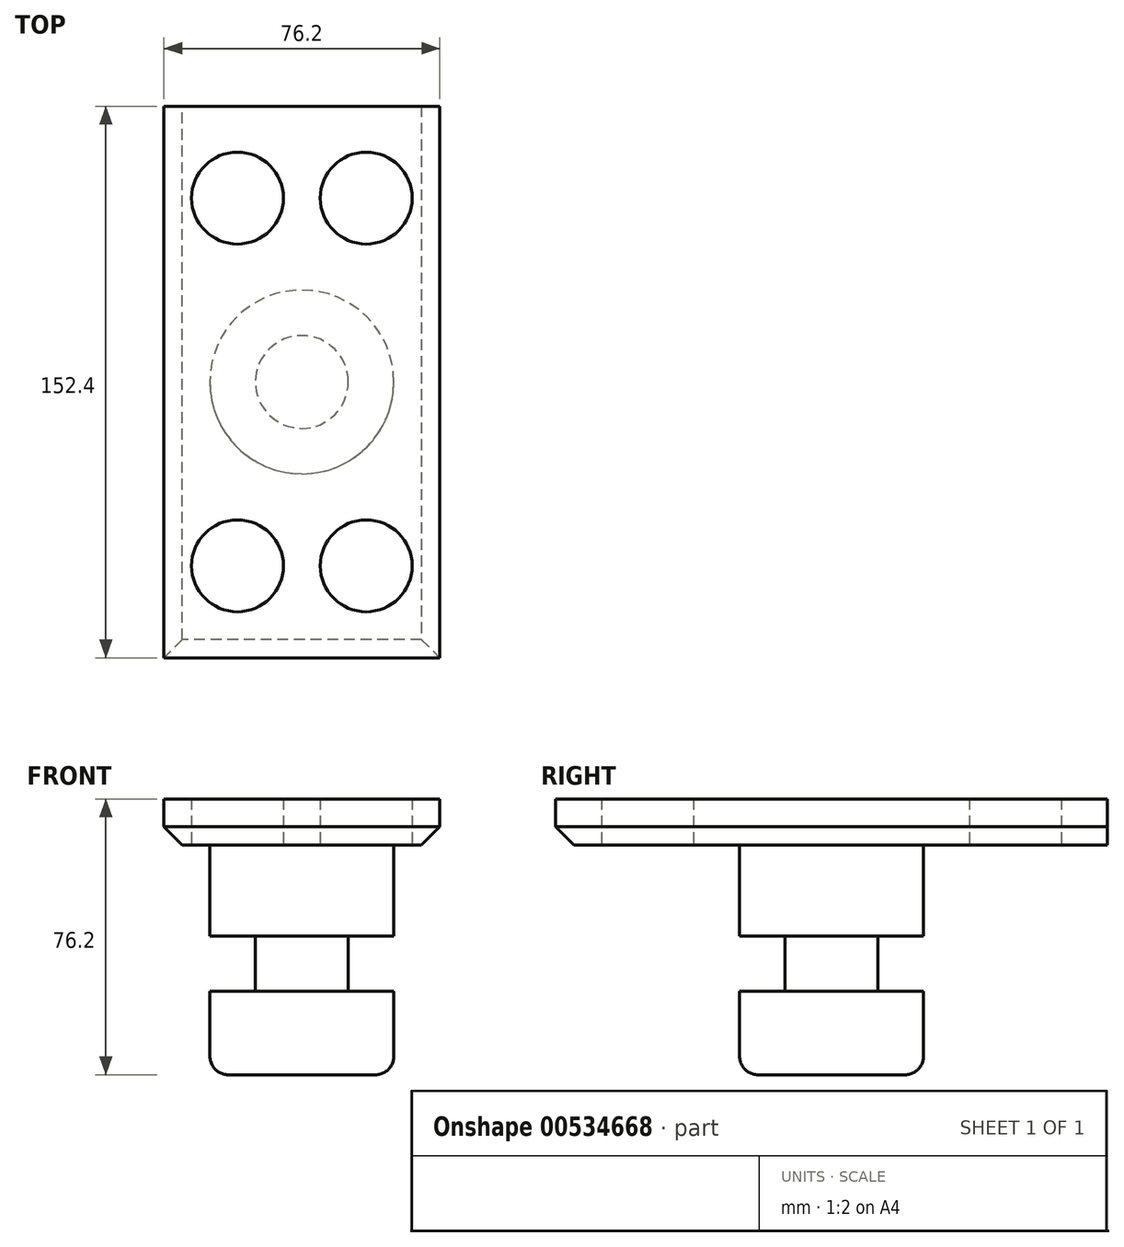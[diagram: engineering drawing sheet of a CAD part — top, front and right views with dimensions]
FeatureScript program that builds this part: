
annotation { "Feature Type Name" : "Feature", "Feature Type Description" : "" }
export const myFeature = defineFeature(function(context is Context, id is Id, definition is map)
    precondition{}
    {
        {
            var Q0;
            Q0=qCreatedBy(makeId("Top.planeOp"),FACE);
            var sketch = newSketch(context, id + "F0", { "sketchPlane" : qUnion([Q0])});
            skLineSegment(sketch, "E0.bottom", {"start": v(38.1, 76.2) * mm, "end": v(-38.1, 76.2) * mm});
            skLineSegment(sketch, "E0.top", {"start": v(38.1, -76.2) * mm, "end": v(-38.1, -76.2) * mm});
            skLineSegment(sketch, "E0.left", {"start": v(38.1, 76.2) * mm, "end": v(38.1, -76.2) * mm});
            skLineSegment(sketch, "E0.right", {"start": v(-38.1, 76.2) * mm, "end": v(-38.1, -76.2) * mm});
            skPoint(sketch, "E0.middle", {"position": v(0, 0) * mm});
            skSolve(sketch);
        }
        {
            var Q0;
            Q0 = qSketchRegion(id + "F0", true);
            extrude(context, id + "F1", {"entities" : qUnion([Q0]), "depth" : 12.7 * mm, "offsetDistance" : 25.4 * mm});
        }
        {
            var Q0;
            Q0=qCreatedBy(makeId("Top.planeOp"),FACE);
            var sketch = newSketch(context, id + "F2", { "sketchPlane" : qUnion([Q0])});
            skCircle(sketch, "E1", {"center": v(-17.78, 50.8) * mm, "radius": 12.7 * mm});
            skCircle(sketch, "E2", {"center": v(-17.78, -50.8) * mm, "radius": 12.7 * mm});
            skCircle(sketch, "E3", {"center": v(17.78, -50.8) * mm, "radius": 12.7 * mm});
            skCircle(sketch, "E4", {"center": v(17.78, 50.8) * mm, "radius": 12.7 * mm});
            skSolve(sketch);
        }
        {
            var Q0;
            Q0=makeQuery(id+"F2.imprint","IMPRINT",FACE,{"disambiguationData":[TD([[makeQuery(id+"F2.imprint","IMPRINT",EDGE,{"derivedFrom":sQuery(id+"F2.wireOp",EDGE,"E1")}),1.0]])]});
            var Q1;
            Q1=makeQuery(id+"F2.imprint","IMPRINT",FACE,{"disambiguationData":[TD([[makeQuery(id+"F2.imprint","IMPRINT",EDGE,{"derivedFrom":sQuery(id+"F2.wireOp",EDGE,"E4")}),1.0]])]});
            var Q2;
            Q2=makeQuery(id+"F2.imprint","IMPRINT",FACE,{"disambiguationData":[TD([[makeQuery(id+"F2.imprint","IMPRINT",EDGE,{"derivedFrom":sQuery(id+"F2.wireOp",EDGE,"E2")}),1.0]])]});
            var Q3;
            Q3=makeQuery(id+"F2.imprint","IMPRINT",FACE,{"disambiguationData":[TD([[makeQuery(id+"F2.imprint","IMPRINT",EDGE,{"derivedFrom":sQuery(id+"F2.wireOp",EDGE,"E3")}),1.0]])]});
            extrude(context, id + "F3", {"entities" : qUnion([Q0, Q1, Q2, Q3]), "operationType" : NewBodyOperationType.REMOVE, "endBound" : BoundingType.UP_TO_NEXT, "depth" : 25.4 * mm, "offsetDistance" : 25.4 * mm});
        }
        {
            var Q0;
            Q0=qCreatedBy(makeId("Right.planeOp"),FACE);
            var sketch = newSketch(context, id + "F4", { "sketchPlane" : qUnion([Q0])});
            skLineSegment(sketch, "E5.bottom", {"start": v(0, -63.5) * mm, "end": v(25.4, -63.5) * mm});
            skLineSegment(sketch, "E5.top", {"start": v(0, 0) * mm, "end": v(25.4, 0) * mm});
            skLineSegment(sketch, "E5.left", {"start": v(0, -63.5) * mm, "end": v(0, 0) * mm});
            skLineSegment(sketch, "E5.right", {"start": v(25.4, -63.5) * mm, "end": v(25.4, 0) * mm});
            skSolve(sketch);
        }
        {
            var Q0;
            Q0=makeQuery(id+"F4.imprint","IMPRINT",FACE,{"disambiguationData":[TD([[makeQuery(id+"F4.imprint","IMPRINT",EDGE,{"derivedFrom":sQuery(id+"F4.wireOp",EDGE,"E5.bottom")}),1.0]])]});
            var Q1;
            Q1=sQuery(id+"F4.wireOp",EDGE,"E5.left");
            revolve(context, id + "F5", {"operationType" : NewBodyOperationType.ADD, "entities" : qUnion([Q0]), "axis" : qUnion([Q1]), "revolveType" : RevolveType.FULL});
        }
        {
            var Q0;
            Q0=qCreatedBy(makeId("Right.planeOp"),FACE);
            var sketch = newSketch(context, id + "F6", { "sketchPlane" : qUnion([Q0])});
            skLineSegment(sketch, "E6.bottom", {"start": v(12.82, -40.48) * mm, "end": v(30.6, -40.48) * mm});
            skLineSegment(sketch, "E6.top", {"start": v(12.82, -25.24) * mm, "end": v(30.6, -25.24) * mm});
            skLineSegment(sketch, "E6.left", {"start": v(12.82, -40.48) * mm, "end": v(12.82, -25.24) * mm});
            skLineSegment(sketch, "E6.right", {"start": v(30.6, -40.48) * mm, "end": v(30.6, -25.24) * mm});
            skSolve(sketch);
        }
        {
            var Q0;
            Q0=makeQuery(id+"F6.imprint","IMPRINT",FACE,{"disambiguationData":[TD([[makeQuery(id+"F6.imprint","IMPRINT",EDGE,{"derivedFrom":sQuery(id+"F6.wireOp",EDGE,"E6.bottom")}),1.0]])]});
            var Q1;
            Q1=makeQuery(id+"F5.opRevolve","SWEPT_FACE",FACE,{"disambiguationData":[OSD([sQuery(id+"F4.wireOp",EDGE,"E5.right")])]});
            revolve(context, id + "F7", {"operationType" : NewBodyOperationType.REMOVE, "entities" : qUnion([Q0]), "axis" : qUnion([Q1]), "revolveType" : RevolveType.FULL});
        }
        {
            var Q0;
            Q0=makeQuery(id+"F5.opRevolve","SWEPT_FACE",FACE,{"disambiguationData":[OSD([sQuery(id+"F4.wireOp",EDGE,"E5.bottom")])]});
            var Q1;
            Q1=makeQuery(id+"F5.opRevolve","SWEPT_EDGE",EDGE,{"disambiguationData":[OSD([sQuery(id+"F4.wireOp",EDGE,"E5.top"),sQuery(id+"F4.wireOp",EDGE,"E5.right")])]});
            fillet(context, id + "F8", {"entities" : qUnion([Q0, Q1]), "radius" : 5.08 * mm, "tangentPropagation" : true, "allowEdgeOverflow" : false});
        }
        {
            var Q0;
            Q0=makeQuery(id+"F1.opExtrude","CAP_EDGE",EDGE,{"disambiguationData":[OSD([sQuery(id+"F0.wireOp",EDGE,"E0.right")])],"isStart":true});
            var Q1;
            Q1=makeQuery(id+"F1.opExtrude","CAP_EDGE",EDGE,{"disambiguationData":[OSD([sQuery(id+"F0.wireOp",EDGE,"E0.top")])],"isStart":true});
            var Q2;
            Q2=makeQuery(id+"F1.opExtrude","CAP_EDGE",EDGE,{"disambiguationData":[OSD([sQuery(id+"F0.wireOp",EDGE,"E0.left")])],"isStart":true});
            chamfer(context, id + "F9", {"entities" : qUnion([Q0, Q1, Q2]), "width" : 5.08 * mm, "tangentPropagation" : true});
        }
    });
